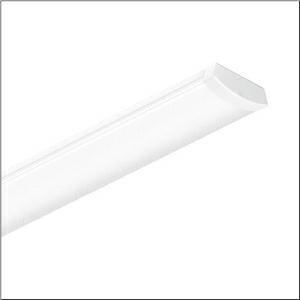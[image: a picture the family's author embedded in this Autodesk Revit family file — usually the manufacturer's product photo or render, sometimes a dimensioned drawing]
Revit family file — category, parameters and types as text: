
# Revit family: siluette_r__21_51ln12mkm40a3g_b368
name_source: partatom
category: Lighting Fixtures
units: mm (PartAtom-declared; Revit-internal decimal feet)

## family parameters
Cut with Voids When Loaded = No
Host = Face
Light Source = No
Part Type = Normal
Room Calculation Point = No
Round Connector Dimension = Use Diameter
Shared = No

## types (1)
- --- (1 x LED, 2980 lm, 20.6 W, 5000K)
    Apparent Load = 21 VA
    CIE Flux Codes = 43 73 92 94 100
    Color Rendering = 80
    Color Temperature = 5000K
    Default Elevation = 1800 mm
    Description = Siluette® 21, office luminaire, primary optical cover: enclosure, of PC, frosted, light emission: direct distribution, primary light characteristic: symmetric, installation type: suspended mounting, surface-mounted, LED, rated luminous flux: 5.010lm, luminous efficacy: 136lm/W, light colour: 830/840/850, colour temperature: 3000/4000/5000K, control gear: ON/OFF Multilumen, with terminal, 4-pole, mains connection: 220..240V, AC, 50/60Hz, rated input power: 37W, control gear: single battery element, housing, of sheet steel, white, length: 1.200mm, width: 152mm, height: 53mm, end cap, of PMMA, white, protection rating (complete): IP44, insulation class (complete): insulation class I (protective earthing), certification: CE, UKCA, protection symbol: D, impact resistance: IK04, permissible operating ambient temperature: +5..+40°C, standard: EN 60598-2-22, contact your sales advisor before using the luminaires in applications with unclear chemical exposure, large temperature fluctuations or condensation-forming humidity, corresponds to IFS (International Featured Standards) requirements for safety and quality in the food industry, packaging unit: 1 piece
    Height = 52 mm  [stored 0.170604 ft]
    Lamp = 1 x LED
    Lamp Light Flux = 2980 lm
    Lamp Power = 20.6 W
    Lamp count = 1
    Length = 1185 mm
    Luminous efficacy = 145 lm/W
    Manufacturer = Siteco
    ModVariant = No
    Model = 51LN12MKM40A3G
    Mounting Place = Ceiling
    Mounting Type = Pendant
    Number of Poles = 1
    OnlyDefault = Yes
    Power Factor = 1
    Product Name = Siluette® 21
    Product group = office luminaire | ceiling pendant
    ProductGroupID = 904
    Protection Class = Protection class I
    Protection Degree = IP 44
    RLX_Detail_Level = 1
    RLX_Emergency_Light_Flux = 0 lm
    RLX_Emergency_Type = 0
    RLX_Emergency_Type_DB = No
    RlxData = <blob elided: 19557 chars, md5=066e2c17>
    Socket = socket
    Standby Power = 0 W
    System Light Flux = 2980 lm
    System Power = 21 W
    Type Comments = individual setting: colour temperature 5000K, luminous flux: 60 % | (OFF | OFF | ON) | 200 mA
    Type Image = l_1296910.jpg
    URL = http://relux.com
    VarID = @adj_059400
    Voltage = 0 V
    Weight = 0.00 kg
    Width = 152 mm

note: [stored X ft] marks values corroborated as IEEE doubles in the binary element streams (Revit-internal decimal feet)

## geometry (parser evidence)
native form markers: Blend x4, Sweep x13
no freeform markers — native parametric forms only
